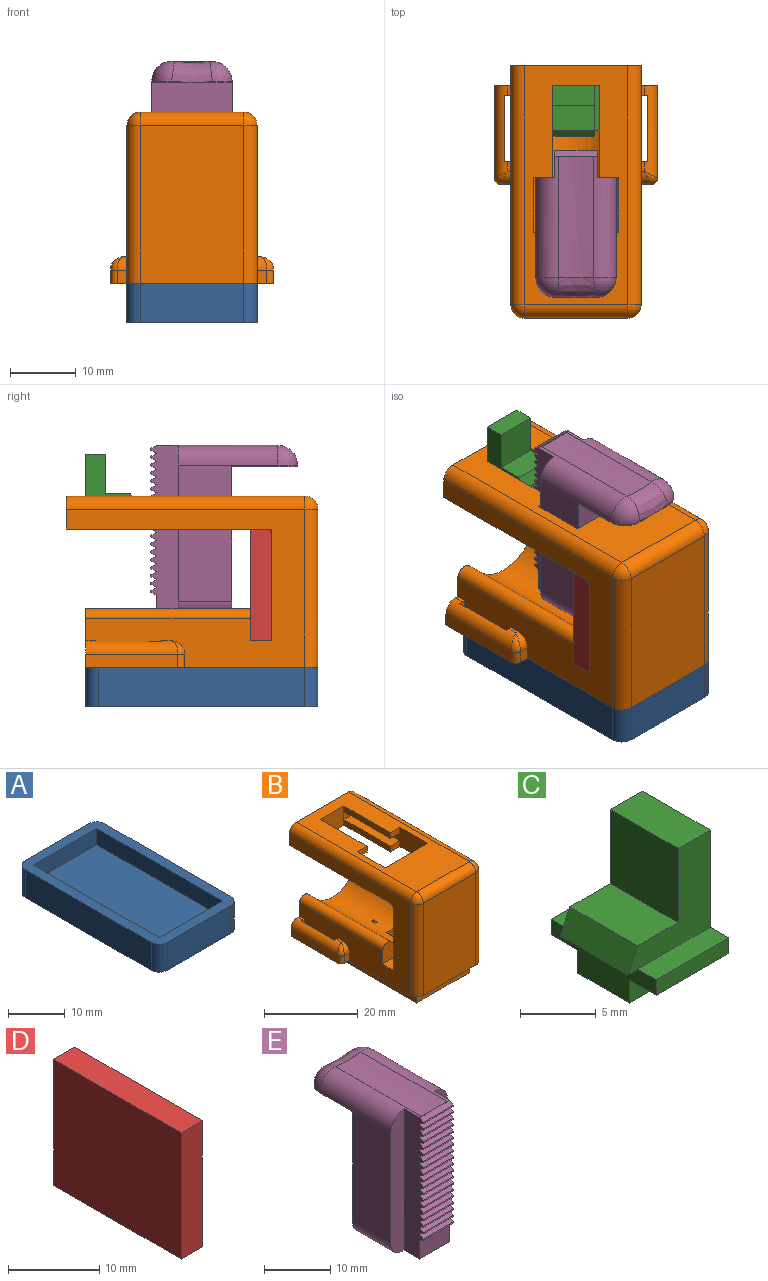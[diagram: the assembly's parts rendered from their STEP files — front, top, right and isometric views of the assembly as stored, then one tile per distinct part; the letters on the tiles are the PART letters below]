
ASSEMBLY  parts=5 mates=4
PART A: 15 faces, bbox 19.8x35.3x6 mm
  f0: plane 15.78x3.5mm, normal (0,-1,0), area 55.2mm2, adj f1,f3,f4,f5
  f1: plane 31.3x3.5mm, normal (1,0,0), area 109.6mm2, adj f0,f2,f4,f5
  f2: plane 15.78x3.5mm, normal (0,1,0), area 55.2mm2, adj f1,f3,f4,f5
  f3: plane 31.3x3.5mm, normal (-1,0,0), area 109.6mm2, adj f0,f2,f4,f5
  f4: plane 31.3x15.78mm, normal (0,0,1), area 493.9mm2, adj f0,f1,f2,f3
  f5: plane 35.3x19.78mm, normal (0,0,1), area 200.9mm2, adj f0,f1,f2,f3,f7,f8,f9,f10
  f6: plane 35.3x19.78mm, normal (0,0,-1), area 694.8mm2, adj f7,f8,f9,f10,f11,f12,f13,f14
  f7: cylinder r=2mm len=6mm, axis (0,0,1), area 18.8mm2, adj f5,f6,f11,f13
  f8: cylinder r=2mm len=6mm, axis (0,0,-1), area 18.8mm2, adj f5,f6,f10,f11
  f9: cylinder r=2mm len=6mm, axis (0,0,1), area 18.8mm2, adj f5,f6,f10,f14
  f10: plane 15.78x6mm, normal (0,-1,0), area 94.7mm2, adj f5,f6,f8,f9
  f11: plane 31.3x6mm, normal (-1,0,0), area 187.8mm2, adj f5,f6,f7,f8
  f12: cylinder r=2mm len=6mm, axis (0,0,-1), area 18.8mm2, adj f5,f6,f13,f14
  f13: plane 15.78x6mm, normal (0,1,0), area 94.7mm2, adj f5,f6,f7,f12
  f14: plane 31.3x6mm, normal (1,0,0), area 187.8mm2, adj f5,f6,f9,f12
PART B: 94 faces, bbox 24.8x38.3x29 mm
  f0: plane 1.5x0.5mm, normal (0,0,1), area 0.7mm2, adj f12,f19,f50,f91
  f1: plane 1.5x0.5mm, normal (0,0,1), area 0.8mm2, adj f20,f48,f88,f90
  f2: plane 2.89x1.5mm, normal (0,-1,0), area 4.3mm2, adj f6,f54,f58,f79
  f3: plane 13.97x1.5mm, normal (1,0,0), area 20.9mm2, adj f9,f10,f75,f80
  f4: plane 2.89x1.5mm, normal (0,-1,0), area 4.3mm2, adj f6,f56,f57,f76
  f5: plane 13.97x1.5mm, normal (-1,0,0), area 20.9mm2, adj f10,f53,f75,f77
  f6: plane 36.3x15.78mm, normal (0,0,1), area 368.5mm2, adj f2,f4,f42,f54,f55,f56,f57,f58
  f7: plane 24x11.78mm, normal (0,0,-1), area 276.8mm2, adj f15,f16,f17,f18,f33,f34,f35,f36
  f8: cylinder r=7mm len=25mm, axis (0,1,0), area 262.3mm2, adj f13,f19,f21,f22,f23,f25,f26,f27
  f9: plane 2.89x1.5mm, normal (0,-1,0), area 4.3mm2, adj f3,f10,f54,f80
  f10: plane 30.3x19.78mm, normal (0,0,-1), area 395.1mm2, adj f3,f5,f9,f12,f20,f41,f53,f54
  f11: plane 35.3x24.78mm, normal (0,0,-1), area 257.2mm2, adj f12,f19,f20,f30,f31,f32,f37,f38
  f12: plane 36.3x24mm, normal (-1,0,0), area 392.7mm2, adj f0,f10,f11,f13,f19,f24,f40,f41
  f13: plane 9.57x4.87mm, normal (0,-1,0), area 22.7mm2, adj f8,f12,f22,f40,f82
  f14: plane 31.3x15.78mm, normal (0,0,-1), area 211.2mm2, adj f30,f31,f32,f33,f34,f35,f36,f38
  f15: plane 1.5x1.5mm, normal (0,1,0), area 2.2mm2, adj f7,f16,f18,f29
  f16: plane 3.7x1.5mm, normal (1,0,0), area 5.5mm2, adj f7,f15,f17,f29
  f17: plane 1.5x1.5mm, normal (0,-1,0), area 2.2mm2, adj f7,f16,f18,f29
  f18: plane 3.7x1.5mm, normal (-1,0,0), area 5.5mm2, adj f7,f15,f17,f29
  f19: plane 24.78x8.88mm, normal (0,1,0), area 142.9mm2, adj f0,f8,f11,f12,f20,f21,f22,f43
  f20: plane 36.3x24mm, normal (1,0,0), area 392.7mm2, adj f1,f10,f11,f19,f23,f24,f40,f41
  f21: plane 25x2.16mm, normal (-0.71,0,0.71), area 76.5mm2, adj f8,f19,f23,f83
  f22: plane 25x2.61mm, normal (0.71,0,0.71), area 92.1mm2, adj f8,f13,f19,f82
  f23: plane 9.57x4.87mm, normal (0,-1,0), area 22.7mm2, adj f8,f20,f21,f40,f83
  f24: plane 19.78x15.99mm, normal (0,1,0), area 316.3mm2, adj f12,f20,f40,f41
  f25: plane 4.7x0.87mm, normal (-1,0,0), area 4.1mm2, adj f8,f26,f28,f29
  f26: plane 2.5x0.87mm, normal (0,1,0), area 2mm2, adj f8,f25,f27,f29
  f27: plane 4.7x0.87mm, normal (1,0,0), area 4.1mm2, adj f8,f26,f28,f29
  f28: plane 2.5x0.87mm, normal (0,-1,0), area 2mm2, adj f8,f25,f27,f29
  f29: plane 4.7x2.5mm, normal (0,0,1), area 6.2mm2, adj f15,f16,f17,f18,f25,f26,f27,f28
  f30: plane 31.3x3mm, normal (-1,0,0), area 93.9mm2, adj f11,f14,f32,f38
  f31: plane 31.3x3mm, normal (1,0,0), area 93.9mm2, adj f11,f14,f32,f38
  f32: plane 15.78x3mm, normal (0,1,0), area 47.3mm2, adj f11,f14,f30,f31
  f33: plane 11.78x4.74mm, normal (0,1,0), area 55.8mm2, adj f7,f14,f34,f36
  f34: plane 24x4.74mm, normal (1,0,0), area 113.8mm2, adj f7,f14,f33,f35
  f35: plane 11.78x4.74mm, normal (0,-1,0), area 55.8mm2, adj f7,f14,f34,f36
  f36: plane 24x4.74mm, normal (-1,0,0), area 113.8mm2, adj f7,f14,f33,f35
  f37: plane 24x15.78mm, normal (0,-1,0), area 378.7mm2, adj f11,f42,f68,f71
  f38: plane 15.78x3mm, normal (0,-1,0), area 47.3mm2, adj f11,f14,f30,f31
  f39: plane 0.64x0.01mm, normal (0,1,0), area 0mm2, adj f8,f40
  f40: plane 19.78x3.3mm, normal (0,0,1), area 65.3mm2, adj f12,f13,f20,f23,f24,f39
  f41: cylinder r=1mm len=19.78mm, axis (-1,0,0), area 31.1mm2, adj f10,f12,f20,f24
  f42: cylinder r=2mm len=15.78mm, axis (-1,0,0), area 49.6mm2, adj f6,f37,f69,f72
  f43: plane 1.5x0.5mm, normal (0,0,1), area 0.8mm2, adj f19,f20,f47,f88
  f44: plane 2x1.5mm, normal (0,-1,0), area 3mm2, adj f11,f20,f86,f90
  f45: plane 1.5x0.5mm, normal (0,0,1), area 0.7mm2, adj f12,f52,f91,f93
  f46: plane 2x1.5mm, normal (0,-1,0), area 3mm2, adj f11,f12,f87,f93
  f47: plane 4x1mm, normal (0,-1,0), area 4mm2, adj f11,f20,f43,f49,f88
  f48: plane 4x1mm, normal (0,1,0), area 4mm2, adj f1,f11,f20,f49,f88
  f49: plane 10x3.94mm, normal (-1,0,0), area 39.4mm2, adj f11,f47,f48,f88
  f50: plane 4x1mm, normal (0,-1,0), area 4mm2, adj f0,f11,f12,f51,f91
  f51: plane 10x3.94mm, normal (1,0,0), area 39.4mm2, adj f11,f50,f52,f91
  f52: plane 4x1mm, normal (0,1,0), area 4mm2, adj f11,f12,f45,f51,f91
  f53: plane 2.89x1.5mm, normal (0,-1,0), area 4.3mm2, adj f5,f10,f56,f77
  f54: plane 22.3x5mm, normal (1,0,0), area 69.6mm2, adj f2,f6,f9,f10,f55,f79,f80,f81
  f55: plane 12.78x5mm, normal (0,1,0), area 63.9mm2, adj f6,f10,f54,f56
  f56: plane 22.3x5mm, normal (-1,0,0), area 69.6mm2, adj f4,f6,f10,f53,f55,f76,f77,f78
  f57: plane 13.97x1.5mm, normal (-1,0,0), area 21mm2, adj f4,f6,f75,f76
  f58: plane 13.97x1.5mm, normal (1,0,0), area 21mm2, adj f2,f6,f75,f79
  f59: plane 1.15x0.32mm, normal (-1,0,0), area 0.4mm2, adj f8,f60,f62,f63
  f60: plane 0.65x0.32mm, normal (0,1,0), area 0.2mm2, adj f8,f59,f61,f63
  f61: plane 1.15x0.32mm, normal (1,0,0), area 0.4mm2, adj f8,f60,f62,f63
  f62: plane 0.65x0.32mm, normal (0,-1,0), area 0.2mm2, adj f8,f59,f61,f63
  f63: plane 1.15x0.65mm, normal (0,0,1), area 0.4mm2, adj f59,f60,f61,f62,f64,f65,f66,f67
  f64: plane 1.95x0.39mm, normal (0,1,0), area 0.8mm2, adj f7,f63,f65,f67
  f65: plane 1.95x0.89mm, normal (-1,0,0), area 1.7mm2, adj f7,f63,f64,f66
  f66: plane 1.95x0.39mm, normal (0,-1,0), area 0.8mm2, adj f7,f63,f65,f67
  f67: plane 1.95x0.89mm, normal (1,0,0), area 1.7mm2, adj f7,f63,f64,f66
  f68: cylinder r=2mm len=24mm, axis (0,0,-1), area 75.4mm2, adj f11,f20,f37,f69
  f69: sphere r=2mm, area 6.3mm2, adj f42,f68,f70
  f70: cylinder r=2mm len=36.3mm, axis (0,-1,0), area 114mm2, adj f6,f20,f69,f74
  f71: cylinder r=2mm len=24mm, axis (0,0,1), area 75.4mm2, adj f11,f12,f37,f72
  f72: sphere r=2mm, area 6.3mm2, adj f42,f71,f73
  f73: cylinder r=2mm len=36.3mm, axis (0,1,0), area 114mm2, adj f6,f12,f72,f74
  f74: plane 19.78x5mm, normal (0,1,0), area 97.2mm2, adj f6,f10,f12,f20,f70,f73
  f75: plane 7x5mm, normal (0,-1,0), area 35mm2, adj f3,f5,f6,f10,f57,f58,f78,f81
  f76: plane 13.97x2.89mm, normal (0,0,-1), area 40.4mm2, adj f4,f56,f57,f78
  f77: plane 13.97x2.89mm, normal (0,0,1), area 40.4mm2, adj f5,f53,f56,f78
  f78: plane 2.89x2mm, normal (0,-1,0), area 5.8mm2, adj f56,f75,f76,f77
  f79: plane 13.97x2.89mm, normal (0,0,-1), area 40.4mm2, adj f2,f54,f58,f81
  f80: plane 13.97x2.89mm, normal (0,0,1), area 40.4mm2, adj f3,f9,f54,f81
  f81: plane 2.89x2mm, normal (0,-1,0), area 5.8mm2, adj f54,f75,f79,f80
  f82: cylinder r=1.5mm len=25mm, axis (0,1,0), area 88.4mm2, adj f12,f13,f19,f22
  f83: cylinder r=1.5mm len=25mm, axis (0,1,0), area 88.4mm2, adj f19,f20,f21,f23
  f84: plane 14x2mm, normal (1,0,0), area 28mm2, adj f11,f19,f86,f88
  f85: plane 14x2mm, normal (-1,0,0), area 28mm2, adj f11,f19,f87,f91
  f86: cylinder r=1mm len=2mm, axis (0,0,1), area 3.1mm2, adj f11,f44,f84,f89
  f87: cylinder r=1mm len=2mm, axis (0,0,-1), area 3.1mm2, adj f11,f46,f85,f92
  f88: cylinder r=2mm len=14mm, axis (0,1,0), area 37.4mm2, adj f1,f19,f43,f47,f48,f49,f84,f89
  f89: bspline ~2.1x2mm, area 3.3mm2, adj f86,f88,f90
  f90: cylinder r=2mm len=2mm, axis (1,0,0), area 3.1mm2, adj f1,f20,f44,f89
  f91: cylinder r=2mm len=14mm, axis (0,-1,0), area 37.4mm2, adj f0,f19,f45,f50,f51,f52,f85,f92
  f92: bspline ~2.39x2mm, area 3.3mm2, adj f87,f91,f93
  f93: cylinder r=2mm len=2mm, axis (-1,0,0), area 3.1mm2, adj f12,f45,f46,f92
PART C: 18 faces, bbox 7.7x9.8x11 mm
  f0: plane 9.84x3.13mm, normal (-1,0,0), area 21.1mm2, adj f1,f3,f4,f6,f9,f11,f12,f13
  f1: plane 6.8x1.75mm, normal (0,0,1), area 11.9mm2, adj f0,f2,f14,f16
  f2: plane 11x9.84mm, normal (1,0,0), area 71.3mm2, adj f1,f3,f4,f6,f10,f11,f12,f13
  f3: plane 6.8x1.88mm, normal (0,-1,0), area 12.7mm2, adj f0,f2,f6,f12
  f4: plane 6.8x1.88mm, normal (0,1,0), area 12.7mm2, adj f0,f2,f6,f13
  f5: plane 6.34x3.8mm, normal (0,0,1), area 24.1mm2, adj f7,f8,f16,f17
  f6: plane 6.8x4.84mm, normal (0,0,-1), area 32.9mm2, adj f0,f2,f3,f4
  f7: plane 6.34x6mm, normal (-1,0,0), area 38mm2, adj f5,f10,f16,f17
  f8: plane 6.34x1.92mm, normal (-0.91,0,0.42), area 13.4mm2, adj f5,f9,f16,f17
  f9: plane 6.34x0.9mm, normal (0,0,-1), area 5.7mm2, adj f0,f8,f16,f17
  f10: plane 6.34x3mm, normal (0,0,1), area 19mm2, adj f2,f7,f16,f17
  f11: plane 6.8x1.75mm, normal (0,0,1), area 11.9mm2, adj f0,f2,f15,f17
  f12: plane 6.8x2.5mm, normal (0,0,-1), area 17mm2, adj f0,f2,f3,f14
  f13: plane 6.8x2.5mm, normal (0,0,-1), area 17mm2, adj f0,f2,f4,f15
  f14: plane 6.8x1.25mm, normal (0,-1,0), area 8.5mm2, adj f0,f1,f2,f12
  f15: plane 6.8x1.25mm, normal (0,1,0), area 8.5mm2, adj f0,f2,f11,f13
  f16: plane 7.92x7.7mm, normal (0,-1,0), area 31.6mm2, adj f0,f1,f2,f5,f7,f8,f9,f10
  f17: plane 7.92x7.7mm, normal (0,1,0), area 31.6mm2, adj f0,f2,f5,f7,f8,f9,f10,f11
PART D: 6 faces, bbox 3.3x19.8x16.9 mm
  f0: plane 19.78x3.3mm, normal (0,0,1), area 65.3mm2, adj f1,f3,f4,f5
  f1: plane 19.78x16.9mm, normal (-1,0,0), area 334.3mm2, adj f0,f2,f4,f5
  f2: plane 19.78x3.3mm, normal (0,0,-1), area 65.3mm2, adj f1,f3,f4,f5
  f3: plane 19.78x16.9mm, normal (1,0,0), area 334.3mm2, adj f0,f2,f4,f5
  f4: plane 16.9x3.3mm, normal (0,-1,0), area 55.8mm2, adj f0,f1,f2,f3
  f5: plane 16.9x3.3mm, normal (0,1,0), area 55.8mm2, adj f0,f1,f2,f3
PART E: 81 faces, bbox 12.2x22.4x26.7 mm
  f0: plane 1.96x0.18mm, normal (0,1,0), area 0.1mm2, adj f5,f55,f57
  f1: extruded ~18.45x5.38mm, area 99.6mm2, adj f10,f53,f54,f57
  f2: plane 11.45x7.2mm, normal (0,0,-1), area 79.9mm2, adj f3,f4,f8,f9,f51,f52,f79,f80
  f3: plane 23x12.2mm, normal (0,1,0), area 277.9mm2, adj f2,f5,f49,f50,f79,f80
  f4: plane 26.17x2.89mm, normal (0,-1,0), area 72.4mm2, adj f2,f50,f51,f53,f80
  f5: plane 12.24x10.04mm, normal (0,0,-1), area 118.1mm2, adj f0,f3,f6,f49,f50,f55,f57,f59
  f6: plane 2.32x0.23mm, normal (0,1,0), area 0.2mm2, adj f5,f57,f59
  f7: plane 0.37x0.01mm, normal (0,-1,0), area 0mm2, adj f11,f52,f54
  f8: plane 6.42x3.41mm, normal (0,-1,0), area 21.9mm2, adj f2,f48,f51,f52
  f9: plane 26.22x2.89mm, normal (0,-1,0), area 72.5mm2, adj f2,f49,f52,f54,f79
  f10: plane 6.05x0.35mm, normal (0,1,0), area 0.9mm2, adj f1,f11,f51,f53,f54
  f11: plane 6.42x0.85mm, normal (0,-0.5,0.87), area 6.3mm2, adj f7,f10,f51,f52,f60
  f12: plane 6.42x0.85mm, normal (0,-0.5,-0.87), area 6.3mm2, adj f13,f51,f52,f60
  f13: plane 6.42x0.85mm, normal (0,-0.5,0.87), area 6.3mm2, adj f12,f51,f52,f61
  f14: plane 6.42x0.85mm, normal (0,-0.5,-0.87), area 6.3mm2, adj f15,f51,f52,f61
  f15: plane 6.42x0.85mm, normal (0,-0.5,0.87), area 6.3mm2, adj f14,f51,f52,f62
  f16: plane 6.42x0.85mm, normal (0,-0.5,-0.87), area 6.3mm2, adj f17,f51,f52,f62
  f17: plane 6.42x0.85mm, normal (0,-0.5,0.87), area 6.3mm2, adj f16,f51,f52,f63
  f18: plane 6.42x0.85mm, normal (0,-0.5,-0.87), area 6.3mm2, adj f19,f51,f52,f63
  f19: plane 6.42x0.85mm, normal (0,-0.5,0.87), area 6.3mm2, adj f18,f51,f52,f64
  f20: plane 6.42x0.85mm, normal (0,-0.5,-0.87), area 6.3mm2, adj f21,f51,f52,f64
  f21: plane 6.42x0.85mm, normal (0,-0.5,0.87), area 6.3mm2, adj f20,f51,f52,f65
  f22: plane 6.42x0.85mm, normal (0,-0.5,-0.87), area 6.3mm2, adj f23,f51,f52,f65
  f23: plane 6.42x0.85mm, normal (0,-0.5,0.87), area 6.3mm2, adj f22,f51,f52,f66
  f24: plane 6.42x0.85mm, normal (0,-0.5,-0.87), area 6.3mm2, adj f25,f51,f52,f66
  f25: plane 6.42x0.85mm, normal (0,-0.5,0.87), area 6.3mm2, adj f24,f51,f52,f67
  f26: plane 6.42x0.85mm, normal (0,-0.5,-0.87), area 6.3mm2, adj f27,f51,f52,f67
  f27: plane 6.42x0.85mm, normal (0,-0.5,0.87), area 6.3mm2, adj f26,f51,f52,f68
  f28: plane 6.42x0.85mm, normal (0,-0.5,-0.87), area 6.3mm2, adj f29,f51,f52,f68
  f29: plane 6.42x0.85mm, normal (0,-0.5,0.87), area 6.3mm2, adj f28,f51,f52,f69
  f30: plane 6.42x0.85mm, normal (0,-0.5,-0.87), area 6.3mm2, adj f31,f51,f52,f69
  f31: plane 6.42x0.85mm, normal (0,-0.5,0.87), area 6.3mm2, adj f30,f51,f52,f70
  f32: plane 6.42x0.85mm, normal (0,-0.5,-0.87), area 6.3mm2, adj f33,f51,f52,f70
  f33: plane 6.42x0.85mm, normal (0,-0.5,0.87), area 6.3mm2, adj f32,f51,f52,f71
  f34: plane 6.42x0.85mm, normal (0,-0.5,-0.87), area 6.3mm2, adj f35,f51,f52,f71
  f35: plane 6.42x0.85mm, normal (0,-0.5,0.87), area 6.3mm2, adj f34,f51,f52,f72
  f36: plane 6.42x0.85mm, normal (0,-0.5,-0.87), area 6.3mm2, adj f37,f51,f52,f72
  f37: plane 6.42x0.85mm, normal (0,-0.5,0.87), area 6.3mm2, adj f36,f51,f52,f73
  f38: plane 6.42x0.85mm, normal (0,-0.5,-0.87), area 6.3mm2, adj f39,f51,f52,f73
  f39: plane 6.42x0.85mm, normal (0,-0.5,0.87), area 6.3mm2, adj f38,f51,f52,f74
  f40: plane 6.42x0.85mm, normal (0,-0.5,-0.87), area 6.3mm2, adj f41,f51,f52,f74
  f41: plane 6.42x0.85mm, normal (0,-0.5,0.87), area 6.3mm2, adj f40,f51,f52,f75
  f42: plane 6.42x0.85mm, normal (0,-0.5,-0.87), area 6.3mm2, adj f43,f51,f52,f75
  f43: plane 6.42x0.85mm, normal (0,-0.5,0.87), area 6.3mm2, adj f42,f51,f52,f76
  f44: plane 6.42x0.85mm, normal (0,-0.5,-0.87), area 6.3mm2, adj f45,f51,f52,f76
  f45: plane 6.42x0.85mm, normal (0,-0.5,0.87), area 6.3mm2, adj f44,f51,f52,f77
  f46: plane 6.42x0.85mm, normal (0,-0.5,-0.87), area 6.3mm2, adj f47,f51,f52,f77
  f47: plane 6.42x0.85mm, normal (0,-0.5,0.87), area 6.3mm2, adj f46,f51,f52,f78
  f48: plane 6.42x0.85mm, normal (0,-0.5,-0.87), area 6.3mm2, adj f8,f51,f52,f78
  f49: plane 20.72x15.15mm, normal (1,0,0), area 170.4mm2, adj f3,f5,f9,f54,f59,f79
  f50: plane 20.67x15.15mm, normal (-1,0,0), area 169.6mm2, adj f3,f4,f5,f53,f55,f80
  f51: plane 26.21x4.22mm, normal (-1,0,0), area 98.1mm2, adj f2,f4,f8,f10,f11,f12,f13,f14
  f52: plane 26.22x4.22mm, normal (1,0,0), area 98.2mm2, adj f2,f7,f8,f9,f11,f12,f13,f14
  f53: cylinder r=3mm len=18.45mm, axis (0,1,0), area 78.9mm2, adj f1,f4,f10,f50,f51,f56
  f54: cylinder r=3mm len=18.45mm, axis (0,1,0), area 79.8mm2, adj f1,f7,f9,f10,f49,f52,f58
  f55: cylinder r=3mm len=3mm, axis (0,0,1), area 0.8mm2, adj f0,f5,f50,f56
  f56: sphere r=3mm, area 15.3mm2, adj f53,f55,f57
  f57: bspline ~11.22x3.65mm, area 26.8mm2, adj f0,f1,f5,f6,f56,f58
  f58: sphere r=3mm, area 10.3mm2, adj f54,f57,f59
  f59: cylinder r=3mm len=3mm, axis (0,0,-1), area 1mm2, adj f5,f6,f49,f58
  f60: cylinder r=0.12mm len=6.42mm, axis (1,0,0), area 1.7mm2, adj f11,f12,f51,f52
  f61: cylinder r=0.12mm len=6.42mm, axis (1,0,0), area 1.7mm2, adj f13,f14,f51,f52
  f62: cylinder r=0.12mm len=6.42mm, axis (1,0,0), area 1.7mm2, adj f15,f16,f51,f52
  f63: cylinder r=0.12mm len=6.42mm, axis (1,0,0), area 1.7mm2, adj f17,f18,f51,f52
  f64: cylinder r=0.12mm len=6.42mm, axis (1,0,0), area 1.7mm2, adj f19,f20,f51,f52
  f65: cylinder r=0.12mm len=6.42mm, axis (1,0,0), area 1.7mm2, adj f21,f22,f51,f52
  f66: cylinder r=0.12mm len=6.42mm, axis (1,0,0), area 1.7mm2, adj f23,f24,f51,f52
  f67: cylinder r=0.12mm len=6.42mm, axis (1,0,0), area 1.7mm2, adj f25,f26,f51,f52
  f68: cylinder r=0.12mm len=6.42mm, axis (1,0,0), area 1.7mm2, adj f27,f28,f51,f52
  f69: cylinder r=0.12mm len=6.42mm, axis (1,0,0), area 1.7mm2, adj f29,f30,f51,f52
  f70: cylinder r=0.12mm len=6.42mm, axis (1,0,0), area 1.7mm2, adj f31,f32,f51,f52
  f71: cylinder r=0.12mm len=6.42mm, axis (1,0,0), area 1.7mm2, adj f33,f34,f51,f52
  f72: cylinder r=0.12mm len=6.42mm, axis (1,0,0), area 1.7mm2, adj f35,f36,f51,f52
  f73: cylinder r=0.12mm len=6.42mm, axis (1,0,0), area 1.7mm2, adj f37,f38,f51,f52
  f74: cylinder r=0.12mm len=6.42mm, axis (1,0,0), area 1.7mm2, adj f39,f40,f51,f52
  f75: cylinder r=0.12mm len=6.42mm, axis (1,0,0), area 1.7mm2, adj f41,f42,f51,f52
  f76: cylinder r=0.12mm len=6.42mm, axis (1,0,0), area 1.7mm2, adj f43,f44,f51,f52
  f77: cylinder r=0.12mm len=6.42mm, axis (1,0,0), area 1.7mm2, adj f45,f46,f51,f52
  f78: cylinder r=0.12mm len=6.42mm, axis (1,0,0), area 1.7mm2, adj f47,f48,f51,f52
  f79: cylinder r=2.5mm len=8.15mm, axis (0,1,0), area 32mm2, adj f2,f3,f9,f49
  f80: cylinder r=2.5mm len=8.15mm, axis (0,-1,0), area 32mm2, adj f2,f3,f4,f50
PLACE A rot(axis=(0,-1,0),0deg) t=(12.19,6.89,-8.47)mm fixed
PLACE B rot(axis=(0,-1,0),0deg) t=(3.47,22.7,-5.47)mm fixed
PLACE C rot(axis=(0,0,1),90deg) t=(7,13.17,18.9)mm
PLACE D rot(axis=(0,0,1),90deg) t=(3.47,-2.09,4.44)mm
PLACE E rot(axis=(0,0,-1),180deg) t=(16.77,45.01,5.03)mm
MATE fastened D.f1 <-> B.f24  axis (0,-1,0) through (23.25,-5.6,1.53)mm
MATE slider E.f5 <-> A.f4  axis (0,0,-1) through (13.36,-4.35,28.03)mm
MATE fastened A.f9 <-> B.f68  axis (0,0,1) through (21.25,-10.6,-2.47)mm
MATE slider C.f2 <-> B.f75  axis (0,1,0) through (9.86,22.7,22.03)mm
